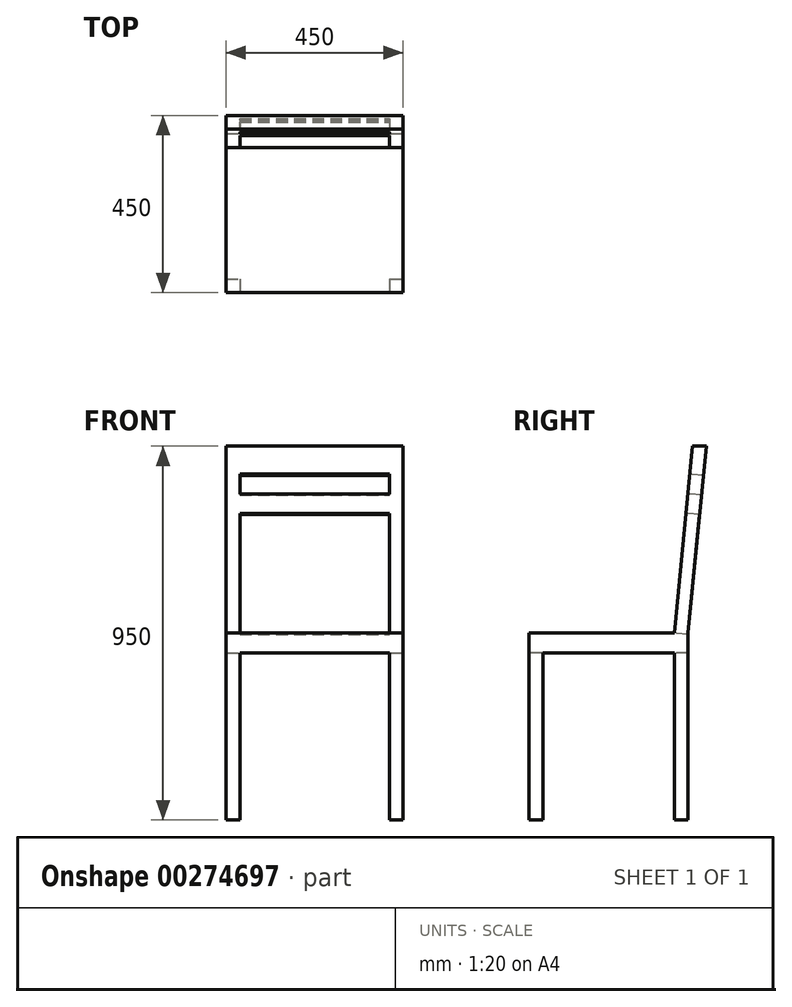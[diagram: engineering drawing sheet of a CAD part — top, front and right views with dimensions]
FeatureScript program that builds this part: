
annotation { "Feature Type Name" : "Feature", "Feature Type Description" : "" }
export const myFeature = defineFeature(function(context is Context, id is Id, definition is map)
    precondition{}
    {
        {
            var Q0;
            Q0=qCreatedBy(makeId("Top.planeOp"),FACE);
            var sketch = newSketch(context, id + "F0", { "sketchPlane" : qUnion([Q0])});
            skLineSegment(sketch, "E0.bottom", {"start": v(225, 225) * mm, "end": v(-225, 225) * mm});
            skLineSegment(sketch, "E0.top", {"start": v(225, -225) * mm, "end": v(-225, -225) * mm});
            skLineSegment(sketch, "E0.left", {"start": v(225, 225) * mm, "end": v(225, -225) * mm});
            skLineSegment(sketch, "E0.right", {"start": v(-225, 225) * mm, "end": v(-225, -225) * mm});
            skPoint(sketch, "E0.middle", {"position": v(0, 0) * mm});
            skSolve(sketch);
        }
        {
            var Q0;
            Q0=qSketchRegion(id+"F0",true);
            extrude(context, id + "F1", {"entities" : qUnion([Q0]), "depth" : 950 * mm});
        }
        {
            var Q0;
            Q0=makeQuery(id+"F1.opExtrude","SWEPT_FACE",FACE,{"disambiguationData":[OSD([sQuery(id+"F0.wireOp",EDGE,"E0.left")])]});
            var sketch = newSketch(context, id + "F2", { "sketchPlane" : qUnion([Q0])});
            skLineSegment(sketch, "E1.bottom", {"start": v(-225, 475) * mm, "end": v(225, 475) * mm});
            skLineSegment(sketch, "E1.top", {"start": v(-225, 425) * mm, "end": v(225, 425) * mm});
            skLineSegment(sketch, "E1.left", {"start": v(-225, 475) * mm, "end": v(-225, 425) * mm});
            skLineSegment(sketch, "E1.right", {"start": v(225, 475) * mm, "end": v(225, 425) * mm});
            skLineSegment(sketch, "E2", {"start": v(225, 950) * mm, "end": v(178.9, 475) * mm});
            skLineSegment(sketch, "E3", {"start": v(190, 950) * mm, "end": v(143.9, 475) * mm});
            skLineSegment(sketch, "E4", {"start": v(143.9, 475) * mm, "end": v(143.9, 0) * mm});
            skLineSegment(sketch, "E5", {"start": v(178.9, 475) * mm, "end": v(178.9, 0) * mm});
            skLineSegment(sketch, "E6.bottom", {"start": v(-225, 425) * mm, "end": v(-190, 425) * mm});
            skLineSegment(sketch, "E6.top", {"start": v(-225, 0) * mm, "end": v(-190, 0) * mm});
            skLineSegment(sketch, "E6.left", {"start": v(-225, 425) * mm, "end": v(-225, 0) * mm});
            skLineSegment(sketch, "E6.right", {"start": v(-190, 425) * mm, "end": v(-190, 0) * mm});
            skSolve(sketch);
        }
        {
            var Q0;
            {var subQ0=sQuery(id+"F2.wireOp",EDGE,"E1.right");Q0=makeQuery(id+"F2.imprint","IMPRINT",FACE,{"disambiguationData":[TD([[makeQuery(id+"F2.imprint","IMPRINT",EDGE,{"derivedFrom":subQ0}),-1.0]])]});}
            var Q1;
            {var subQ4=sQuery(id+"F2.wireOp",EDGE,"E3");Q1=makeQuery(id+"F2.imprint","IMPRINT",FACE,{"disambiguationData":[TD([[makeQuery(id+"F2.imprint","IMPRINT",EDGE,{"derivedFrom":subQ4}),-1.0]])]});}
            var Q2;
            {var subQ4=sQuery(id+"F2.wireOp",EDGE,"E2");Q2=makeQuery(id+"F2.imprint","IMPRINT",FACE,{"disambiguationData":[TD([[makeQuery(id+"F2.imprint","IMPRINT",EDGE,{"derivedFrom":subQ4}),1.0]])]});}
            var Q3;
            {var subQ0=sQuery(id+"F2.wireOp",EDGE,"E6.right");Q3=makeQuery(id+"F2.imprint","IMPRINT",FACE,{"disambiguationData":[TD([[makeQuery(id+"F2.imprint","IMPRINT",EDGE,{"derivedFrom":subQ0}),1.0]])]});}
            var Q4;
            {var subQ1=sQuery(id+"F0.wireOp",EDGE,"E0.left");var subQ4=sQuery(id+"F2.wireOp",EDGE,"E5");var subQ6=makeQuery(id+"F1.opExtrude","CAP_EDGE",EDGE,{"disambiguationData":[OSD([subQ1])],"isStart":true});var subQ7=makeQuery(id+"F2.imprint","INTERSECT",VERTEX,{"derivedFrom":[subQ6,subQ4]});Q4=makeQuery(id+"F2.imprint","IMPRINT",FACE,{"disambiguationData":[TD([[makeQuery(id+"F2.imprint","IMPRINT",EDGE,{"disambiguationData":[TD([[subQ7,1.0]])],"derivedFrom":subQ4}),1.0]])]});}
            extrude(context, id + "F3", {"entities" : qUnion([Q0, Q1, Q2, Q3, Q4]), "operationType" : NewBodyOperationType.REMOVE, "endBound" : BoundingType.THROUGH_ALL, "oppositeDirection" : true, "depth" : 25 * mm});
        }
        {
            var Q0;
            Q0=makeQuery(id+"F3.boolean.opBoolean","COPY",FACE,{"derivedFrom":makeQuery(id+"F3.opExtrude","SWEPT_FACE",FACE,{"disambiguationData":[OSD([sQuery(id+"F2.wireOp",EDGE,"E3")])]})});
            var sketch = newSketch(context, id + "F4", { "sketchPlane" : qUnion([Q0])});
            skLineSegment(sketch, "E7.bottom", {"start": v(-200.57, 921.99) * mm, "end": v(197.94, 921.99) * mm});
            skLineSegment(sketch, "E7.top", {"start": v(-200.57, 847.27) * mm, "end": v(197.94, 847.27) * mm});
            skLineSegment(sketch, "E7.left", {"start": v(-200.57, 921.99) * mm, "end": v(-200.57, 847.27) * mm});
            skLineSegment(sketch, "E7.right", {"start": v(197.94, 921.99) * mm, "end": v(197.94, 847.27) * mm});
            skLineSegment(sketch, "E8.bottom", {"start": v(-200.57, 795.1) * mm, "end": v(200.74, 795.1) * mm});
            skLineSegment(sketch, "E8.top", {"start": v(-200.57, 507.5) * mm, "end": v(200.74, 507.5) * mm});
            skLineSegment(sketch, "E8.left", {"start": v(-200.57, 795.1) * mm, "end": v(-200.57, 507.5) * mm});
            skLineSegment(sketch, "E8.right", {"start": v(200.74, 795.1) * mm, "end": v(200.74, 507.5) * mm});
            skSolve(sketch);
        }
        {
            var Q0;
            Q0=makeQuery(id+"F4.imprint","IMPRINT",FACE,{"disambiguationData":[TD([[makeQuery(id+"F4.imprint","IMPRINT",EDGE,{"derivedFrom":sQuery(id+"F4.wireOp",EDGE,"E7.bottom")}),-1.0]])]});
            var Q1;
            Q1=makeQuery(id+"F4.imprint","IMPRINT",FACE,{"disambiguationData":[TD([[makeQuery(id+"F4.imprint","IMPRINT",EDGE,{"derivedFrom":sQuery(id+"F4.wireOp",EDGE,"E8.bottom")}),-1.0]])]});
            extrude(context, id + "F5", {"entities" : qUnion([Q0, Q1]), "operationType" : NewBodyOperationType.REMOVE, "endBound" : BoundingType.THROUGH_ALL, "depth" : 25 * mm});
        }
        {
            var Q0;
            Q0=makeQuery(id+"F1.opExtrude","SWEPT_FACE",FACE,{"disambiguationData":[OSD([sQuery(id+"F0.wireOp",EDGE,"E0.top")])]});
            var sketch = newSketch(context, id + "F6", { "sketchPlane" : qUnion([Q0])});
            skLineSegment(sketch, "E9", {"start": v(-190, 0) * mm, "end": v(-190, 425) * mm});
            skLineSegment(sketch, "E10", {"start": v(-190, 425) * mm, "end": v(190, 425) * mm});
            skLineSegment(sketch, "E11", {"start": v(190, 425) * mm, "end": v(190, 0) * mm});
            skSolve(sketch);
        }
        {
            var Q0;
            Q0 = qSketchRegion(id + "F6", true);
            var Q1;
            {var subQ0=sQuery(id+"F6.wireOp",EDGE,"E9");Q1=makeQuery(id+"F6.imprint","IMPRINT",FACE,{"disambiguationData":[TD([[makeQuery(id+"F6.imprint","IMPRINT",EDGE,{"derivedFrom":subQ0}),-1.0]])]});}
            extrude(context, id + "F7", {"entities" : qUnion([Q0, Q1]), "operationType" : NewBodyOperationType.REMOVE, "endBound" : BoundingType.THROUGH_ALL, "oppositeDirection" : true, "depth" : 25 * mm});
        }
        {
            var Q0;
            Q0=makeQuery(id+"F3.boolean.opBoolean","COPY",FACE,{"derivedFrom":makeQuery(id+"F3.opExtrude","SWEPT_FACE",FACE,{"disambiguationData":[OSD([sQuery(id+"F2.wireOp",EDGE,"E3")])]})});
            var sketch = newSketch(context, id + "F8", { "sketchPlane" : qUnion([Q0])});
            skLineSegment(sketch, "E12", {"start": v(-190, 486.68) * mm, "end": v(-190, 892.29) * mm});
            skLineSegment(sketch, "E13", {"start": v(-190, 892.29) * mm, "end": v(190, 892.29) * mm});
            skLineSegment(sketch, "E14", {"start": v(190, 892.29) * mm, "end": v(190, 486.68) * mm});
            skLineSegment(sketch, "E15", {"start": v(-190, 842.29) * mm, "end": v(190, 842.29) * mm});
            skLineSegment(sketch, "E16", {"start": v(-190, 792.29) * mm, "end": v(190, 792.29) * mm});
            skSolve(sketch);
        }
        {
            var Q0;
            {var subQ3=sQuery(id+"F8.wireOp",EDGE,"E16");Q0=makeQuery(id+"F8.imprint","IMPRINT",FACE,{"disambiguationData":[TD([[makeQuery(id+"F8.imprint","IMPRINT",EDGE,{"derivedFrom":subQ3}),-1.0]])]});}
            var Q1;
            {var subQ0=sQuery(id+"F8.wireOp",EDGE,"E13");Q1=makeQuery(id+"F8.imprint","IMPRINT",FACE,{"disambiguationData":[TD([[makeQuery(id+"F8.imprint","IMPRINT",EDGE,{"derivedFrom":subQ0}),-1.0]])]});}
            extrude(context, id + "F9", {"entities" : qUnion([Q0, Q1]), "operationType" : NewBodyOperationType.REMOVE, "endBound" : BoundingType.THROUGH_ALL, "oppositeDirection" : true, "depth" : 25 * mm});
        }
    });
